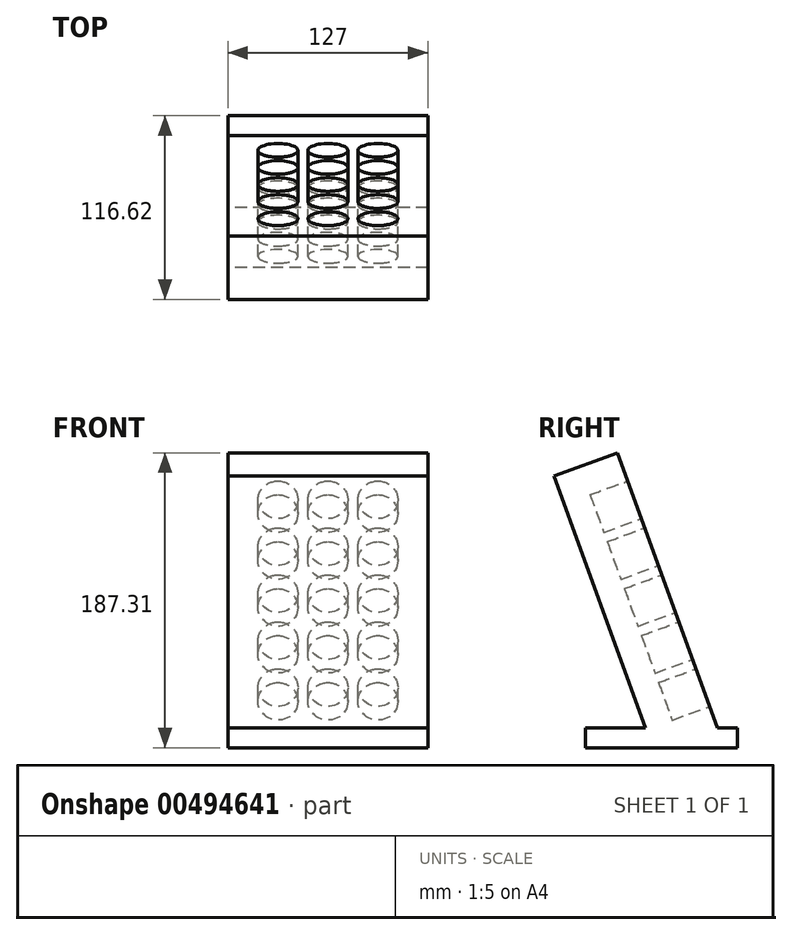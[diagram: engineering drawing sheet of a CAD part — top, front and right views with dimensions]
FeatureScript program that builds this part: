
annotation { "Feature Type Name" : "Feature", "Feature Type Description" : "" }
export const myFeature = defineFeature(function(context is Context, id is Id, definition is map)
    precondition{}
    {
        {
            var Q0;
            Q0=qCreatedBy(makeId("Right.planeOp"),FACE);
            var sketch = newSketch(context, id + "F0", { "sketchPlane" : qUnion([Q0])});
            skLineSegment(sketch, "E0.bottom", {"start": v(-48.26, -6.35) * mm, "end": v(48.26, -6.35) * mm});
            skLineSegment(sketch, "E0.top", {"start": v(-48.26, 6.35) * mm, "end": v(48.26, 6.35) * mm});
            skLineSegment(sketch, "E0.left", {"start": v(-48.26, -6.35) * mm, "end": v(-48.26, 6.35) * mm});
            skLineSegment(sketch, "E0.right", {"start": v(48.26, -6.35) * mm, "end": v(48.26, 6.35) * mm});
            skPoint(sketch, "E0.middle", {"position": v(0, 0) * mm});
            skLineSegment(sketch, "E1", {"start": v(35.56, 6.35) * mm, "end": v(-28, 180.96) * mm});
            skLineSegment(sketch, "E2", {"start": v(-28, 180.96) * mm, "end": v(-68.36, 166.27) * mm});
            skLineSegment(sketch, "E3", {"start": v(-68.36, 166.27) * mm, "end": v(-10.16, 6.35) * mm});
            skSolve(sketch);
        }
        {
            var Q0;
            Q0 = qSketchRegion(id + "F0", true);
            extrude(context, id + "F1", {"entities" : qUnion([Q0]), "depth" : 63.5 * mm, "hasSecondDirection" : true, "secondDirectionOppositeDirection" : true, "secondDirectionDepth" : 63.5 * mm});
        }
        {
            var Q0;
            Q0=makeQuery(id+"F1.opExtrude","SWEPT_FACE",FACE,{"disambiguationData":[OSD([sQuery(id+"F0.wireOp",EDGE,"E1")])]});
            var sketch = newSketch(context, id + "F2", { "sketchPlane" : qUnion([Q0])});
            skLineSegment(sketch, "E4", {"start": v(0, -43.95) * mm, "end": v(0, 190.24) * mm, "construction": true});
            skPoint(sketch, "E4.endSnap0", {"position": v(0, -6.2) * mm});
            skLineSegment(sketch, "E5", {"start": v(-31.75, 197.52) * mm, "end": v(-31.75, -28.78) * mm, "construction": true});
            skLineSegment(sketch, "E6", {"start": v(31.75, 195.68) * mm, "end": v(31.75, -30.78) * mm, "construction": true});
            skLineSegment(sketch, "E7", {"start": v(-63.5, 179.62) * mm, "end": v(157.94, 179.62) * mm, "construction": true});
            skLineSegment(sketch, "E8", {"start": v(-106.83, 0) * mm, "end": v(142.22, 0) * mm, "construction": true});
            skLineSegment(sketch, "E9", {"start": v(131.13, 147.87) * mm, "end": v(-139.65, 147.87) * mm, "construction": true});
            skLineSegment(sketch, "E10", {"start": v(-140.35, 116.12) * mm, "end": v(136.74, 116.12) * mm, "construction": true});
            skLineSegment(sketch, "E11", {"start": v(-143.5, 84.37) * mm, "end": v(162.35, 84.37) * mm, "construction": true});
            skLineSegment(sketch, "E12", {"start": v(153.58, 52.62) * mm, "end": v(-148.76, 52.62) * mm, "construction": true});
            skLineSegment(sketch, "E13", {"start": v(-160.34, 20.87) * mm, "end": v(185.14, 20.87) * mm, "construction": true});
            skCircle(sketch, "E14", {"center": v(-31.75, 147.87) * mm, "radius": 12.7 * mm});
            skCircle(sketch, "E15", {"center": v(0, 147.87) * mm, "radius": 12.7 * mm});
            skCircle(sketch, "E16", {"center": v(31.75, 147.87) * mm, "radius": 12.7 * mm});
            skCircle(sketch, "E17", {"center": v(31.75, 116.12) * mm, "radius": 12.7 * mm});
            skCircle(sketch, "E18", {"center": v(-31.75, 116.12) * mm, "radius": 12.7 * mm});
            skCircle(sketch, "E19", {"center": v(0, 116.12) * mm, "radius": 12.7 * mm});
            skCircle(sketch, "E20", {"center": v(31.75, 84.37) * mm, "radius": 12.7 * mm});
            skCircle(sketch, "E21", {"center": v(0, 84.37) * mm, "radius": 12.7 * mm});
            skCircle(sketch, "E22", {"center": v(-31.75, 84.37) * mm, "radius": 12.7 * mm});
            skCircle(sketch, "E23", {"center": v(0, 52.62) * mm, "radius": 12.7 * mm});
            skCircle(sketch, "E24", {"center": v(31.75, 52.62) * mm, "radius": 12.7 * mm});
            skCircle(sketch, "E25", {"center": v(-31.75, 52.62) * mm, "radius": 12.7 * mm});
            skCircle(sketch, "E26", {"center": v(-31.75, 20.87) * mm, "radius": 12.7 * mm});
            skCircle(sketch, "E27", {"center": v(0, 20.87) * mm, "radius": 12.7 * mm});
            skCircle(sketch, "E28", {"center": v(31.75, 20.87) * mm, "radius": 12.7 * mm});
            skSolve(sketch);
        }
        {
            var Q0;
            Q0 = qSketchRegion(id + "F2", true);
            extrude(context, id + "F3", {"entities" : qUnion([Q0]), "operationType" : NewBodyOperationType.REMOVE, "oppositeDirection" : true, "depth" : 25.4 * mm});
        }
    });
